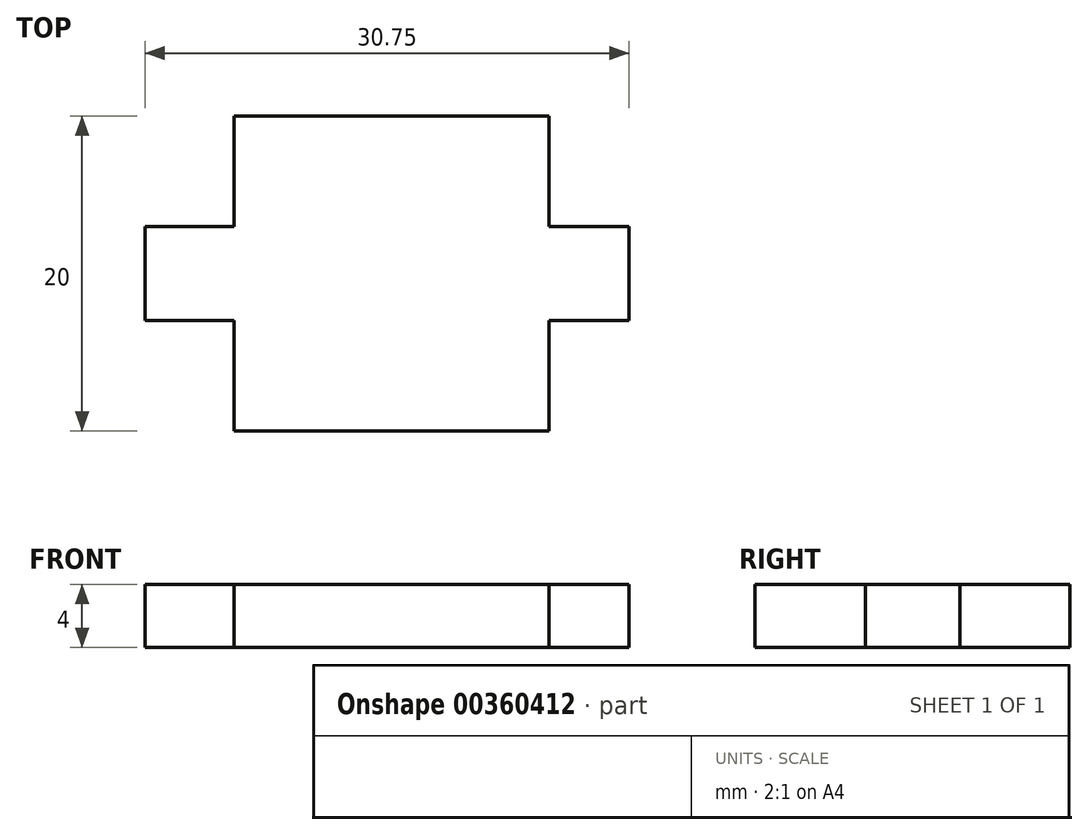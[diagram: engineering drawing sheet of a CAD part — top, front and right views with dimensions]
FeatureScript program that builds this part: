
annotation { "Feature Type Name" : "Feature", "Feature Type Description" : "" }
export const myFeature = defineFeature(function(context is Context, id is Id, definition is map)
    precondition{}
    {
        {
            var Q0;
            Q0=qCreatedBy(makeId("Top.planeOp"),FACE);
            var sketch = newSketch(context, id + "F0", { "sketchPlane" : qUnion([Q0])});
            skLineSegment(sketch, "E0.bottom", {"start": v(-10, 10) * mm, "end": v(10, 10) * mm});
            skLineSegment(sketch, "E0.top", {"start": v(-10, -10) * mm, "end": v(10, -10) * mm});
            skLineSegment(sketch, "E0.left", {"start": v(-10, 10) * mm, "end": v(-10, -10) * mm});
            skLineSegment(sketch, "E0.right", {"start": v(10, 10) * mm, "end": v(10, -10) * mm});
            skPoint(sketch, "E0.middle", {"position": v(0, 0) * mm});
            skLineSegment(sketch, "E1.bottom", {"start": v(-15.65, 3) * mm, "end": v(-10, 3) * mm});
            skLineSegment(sketch, "E1.top", {"start": v(-15.65, -3) * mm, "end": v(-10, -3) * mm});
            skLineSegment(sketch, "E1.left", {"start": v(-15.65, 3) * mm, "end": v(-15.65, -3) * mm});
            skPoint(sketch, "E1.middle", {"position": v(-10, 0) * mm});
            skLineSegment(sketch, "E2.bottom", {"start": v(15.1, 3) * mm, "end": v(10, 3) * mm});
            skLineSegment(sketch, "E2.top", {"start": v(15.1, -3) * mm, "end": v(10, -3) * mm});
            skLineSegment(sketch, "E2.left", {"start": v(15.1, 3) * mm, "end": v(15.1, -3) * mm});
            skPoint(sketch, "E2.middle", {"position": v(10, 0) * mm});
            skSolve(sketch);
        }
        {
            var Q0;
            Q0 = qSketchRegion(id + "F0", true);
            extrude(context, id + "F1", {"entities" : qUnion([Q0]), "depth" : 4 * mm});
        }
    });
